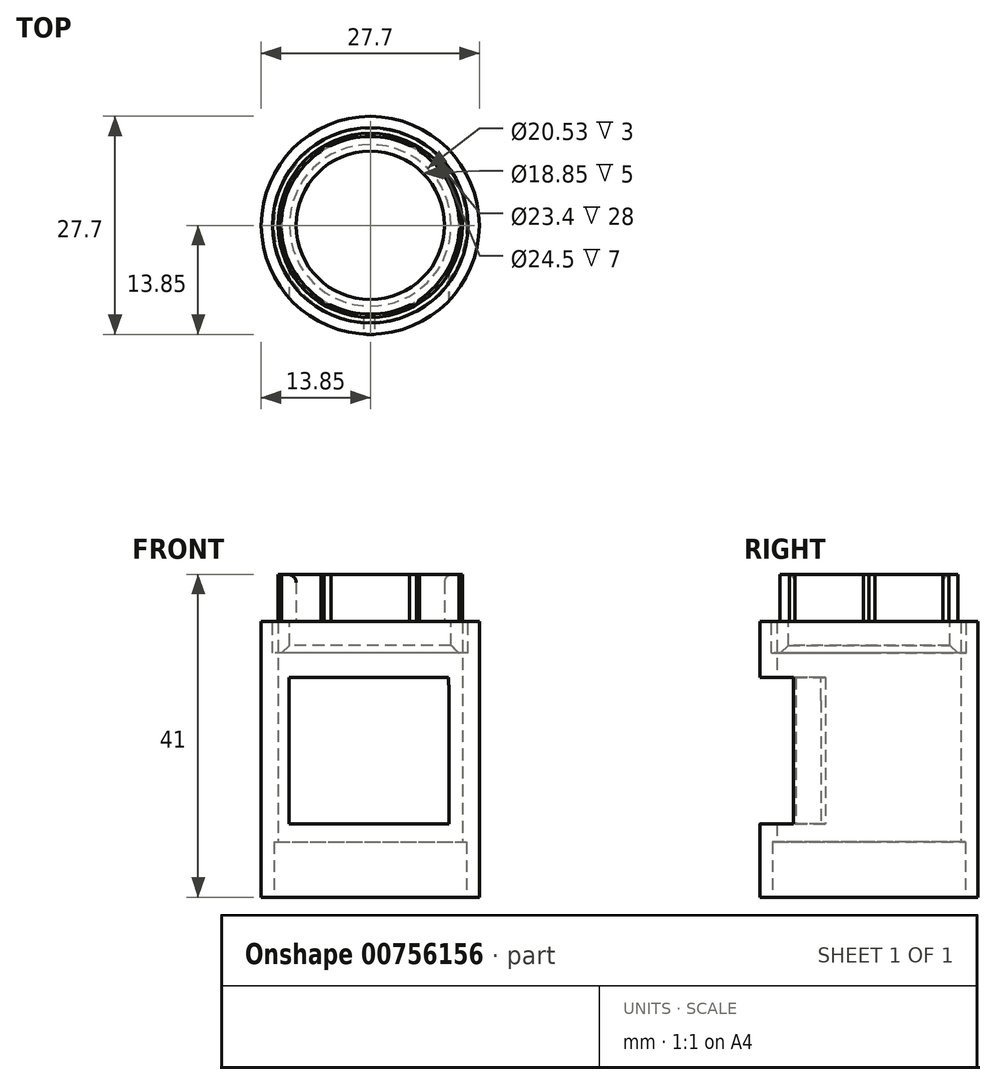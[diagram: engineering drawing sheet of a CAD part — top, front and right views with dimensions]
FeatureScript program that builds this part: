
annotation { "Feature Type Name" : "Feature", "Feature Type Description" : "" }
export const myFeature = defineFeature(function(context is Context, id is Id, definition is map)
    precondition{}
    {
        {
            var Q0;
            Q0=qCreatedBy(makeId("Top.planeOp"),FACE);
            var sketch = newSketch(context, id + "F0", { "sketchPlane" : qUnion([Q0])});
            skCircle(sketch, "E0", {"center": v(0, 0) * mm, "radius": 13.85 * mm});
            skCircle(sketch, "E1", {"center": v(0, 0) * mm, "radius": 11.7 * mm});
            skSolve(sketch);
        }
        {
            var Q0;
            Q0=makeQuery(id+"F0.imprint","IMPRINT",FACE,{"disambiguationData":[TD([[makeQuery(id+"F0.imprint","IMPRINT",EDGE,{"derivedFrom":sQuery(id+"F0.wireOp",EDGE,"E0")}),1.0]])]});
            extrude(context, id + "F1", {"entities" : qUnion([Q0]), "depth" : 35 * mm, "offsetDistance" : 25 * mm});
        }
        {
            var Q0;
            Q0=makeQuery(id+"F1.opExtrude","CAP_FACE",FACE,{"disambiguationData":[OSD([sQuery(id+"F0.wireOp",EDGE,"E0"),sQuery(id+"F0.wireOp",EDGE,"E1")])],"isStart":false});
            var sketch = newSketch(context, id + "F2", { "sketchPlane" : qUnion([Q0])});
            skCircle(sketch, "E2", {"center": v(0, 0) * mm, "radius": 11.3 * mm});
            skCircle(sketch, "E3.cCircle", {"center": v(0, 0) * mm, "radius": 11.7 * mm, "construction": true});
            skLineSegment(sketch, "E3.0", {"start": v(11.7, 0) * mm, "end": v(5.85, -10.13) * mm});
            skLineSegment(sketch, "E3.1", {"start": v(5.85, -10.13) * mm, "end": v(-5.85, -10.13) * mm});
            skLineSegment(sketch, "E3.2", {"start": v(-5.85, -10.13) * mm, "end": v(-11.7, 0) * mm});
            skLineSegment(sketch, "E3.3", {"start": v(-11.7, 0) * mm, "end": v(-5.85, 10.13) * mm});
            skLineSegment(sketch, "E3.4", {"start": v(-5.85, 10.13) * mm, "end": v(5.85, 10.13) * mm});
            skLineSegment(sketch, "E3.5", {"start": v(5.85, 10.13) * mm, "end": v(11.7, 0) * mm});
            skCircle(sketch, "E4", {"center": v(0, 0) * mm, "radius": 9.43 * mm});
            skSolve(sketch);
        }
        {
            var Q0;
            Q0=qSketchRegion(id+"F2",true);
            extrude(context, id + "F3", {"entities" : qUnion([Q0]), "depth" : 6 * mm, "offsetDistance" : 25 * mm});
        }
        {
            var Q0;
            Q0=makeQuery(id+"F1.opExtrude","CAP_FACE",FACE,{"disambiguationData":[OSD([sQuery(id+"F0.wireOp",EDGE,"E0"),sQuery(id+"F0.wireOp",EDGE,"E1")])],"isStart":false});
            var sketch = newSketch(context, id + "F4", { "sketchPlane" : qUnion([Q0])});
            skCircle(sketch, "E5", {"center": v(0, 0) * mm, "radius": 12.4 * mm});
            skCircle(sketch, "E6", {"center": v(0, 0) * mm, "radius": 10.27 * mm});
            skSolve(sketch);
        }
        {
            var Q0;
            Q0=qSketchRegion(id+"F4",true);
            extrude(context, id + "F5", {"entities" : qUnion([Q0]), "oppositeDirection" : true, "depth" : 4 * mm, "offsetDistance" : 25 * mm});
        }
        {
            var Q0;
            Q0=makeQuery(id+"F5.opExtrude","CAP_EDGE",EDGE,{"disambiguationData":[OSD([sQuery(id+"F4.wireOp",EDGE,"E6")])],"isStart":false});
            chamfer(context, id + "F6", {"entities" : qUnion([Q0]), "width" : 1 * mm, "tangentPropagation" : true});
        }
        {
            var Q0;
            Q0=makeQuery(id+"F3.opExtrude","CAP_EDGE",EDGE,{"disambiguationData":[OSD([sQuery(id+"F2.wireOp",EDGE,"E4")])],"isStart":false});
            fillet(context, id + "F7", {"entities" : qUnion([Q0]), "radius" : 1 * mm, "tangentPropagation" : true, "allowEdgeOverflow" : false});
        }
        {
            var Q0;
            Q0=makeQuery(id+"F1.opExtrude","CAP_FACE",FACE,{"disambiguationData":[OSD([sQuery(id+"F0.wireOp",EDGE,"E0"),sQuery(id+"F0.wireOp",EDGE,"E1")])],"isStart":true});
            var sketch = newSketch(context, id + "F8", { "sketchPlane" : qUnion([Q0])});
            skCircle(sketch, "E7", {"center": v(0, 0) * mm, "radius": 12.25 * mm});
            skSolve(sketch);
        }
        {
            var Q0;
            Q0=qSketchRegion(id+"F8",true);
            extrude(context, id + "F9", {"entities" : qUnion([Q0]), "operationType" : NewBodyOperationType.REMOVE, "oppositeDirection" : true, "depth" : 7 * mm, "offsetDistance" : 25 * mm});
        }
        {
            var Q0;
            Q0=qCreatedBy(makeId("Front.planeOp"),FACE);
            cPlane(context, id + "F10", {"entities" : qUnion([Q0]), "cplaneType" : CPlaneType.OFFSET, "offset" : 14 * mm, "width" : 150 * mm, "height" : 150 * mm});
        }
        {
            var Q0;
            Q0=qCreatedBy(id+"F10.planeOp",FACE);
            var sketch = newSketch(context, id + "F11", { "sketchPlane" : qUnion([Q0])});
            skLineSegment(sketch, "E8.bottom", {"start": v(-10.3, 25) * mm, "end": v(9.98, 25) * mm});
            skLineSegment(sketch, "E8.top", {"start": v(-0.87, 9.31) * mm, "end": v(0.55, 9.31) * mm});
            skLineSegment(sketch, "E8.left", {"start": v(-10.3, 25) * mm, "end": v(-10.3, 17.16) * mm});
            skLineSegment(sketch, "E8.right", {"start": v(9.98, 25) * mm, "end": v(9.98, 17.16) * mm});
            skArc(sketch, "E9", {"start": v(-0.87, 9.31) * mm, "mid": v(-0.16, 9.29) * mm, "end": v(0.55, 9.31) * mm});
            skPoint(sketch, "E10.orphan", {"position": v(-10.3, 9.31) * mm});
            skPoint(sketch, "E11.orphan", {"position": v(9.98, 9.31) * mm});
            skLineSegment(sketch, "E12.top", {"start": v(-10.3, 9.31) * mm, "end": v(9.98, 9.31) * mm});
            skLineSegment(sketch, "E12.left", {"start": v(-10.3, 17.16) * mm, "end": v(-10.3, 9.31) * mm});
            skLineSegment(sketch, "E12.right", {"start": v(9.98, 17.16) * mm, "end": v(9.98, 9.31) * mm});
            skSolve(sketch);
        }
        {
            var Q0;
            Q0=qSketchRegion(id+"F11",true);
            extrude(context, id + "F12", {"entities" : qUnion([Q0]), "operationType" : NewBodyOperationType.REMOVE, "oppositeDirection" : true, "depth" : 13 * mm, "offsetDistance" : 25 * mm});
        }
        {
            var Q0;
            Q0=qCreatedBy(id+"F10.planeOp",FACE);
            var sketch = newSketch(context, id + "F13", { "sketchPlane" : qUnion([Q0])});
            skLineSegment(sketch, "E13", {"start": v(-10.3, 25) * mm, "end": v(9.98, 25) * mm});
            skLineSegment(sketch, "E14", {"start": v(-10.3, 25) * mm, "end": v(-10.3, 27.9) * mm});
            skLineSegment(sketch, "E15", {"start": v(-10.3, 27.9) * mm, "end": v(9.96, 27.9) * mm});
            skLineSegment(sketch, "E16", {"start": v(9.96, 27.9) * mm, "end": v(9.98, 25) * mm});
            skSolve(sketch);
        }
        {
            var Q0;
            Q0 = qSketchRegion(id + "F13", true);
            extrude(context, id + "F14", {"entities" : qUnion([Q0]), "operationType" : NewBodyOperationType.REMOVE, "oppositeDirection" : true, "depth" : 10 * mm, "offsetDistance" : 25 * mm});
        }
    });
